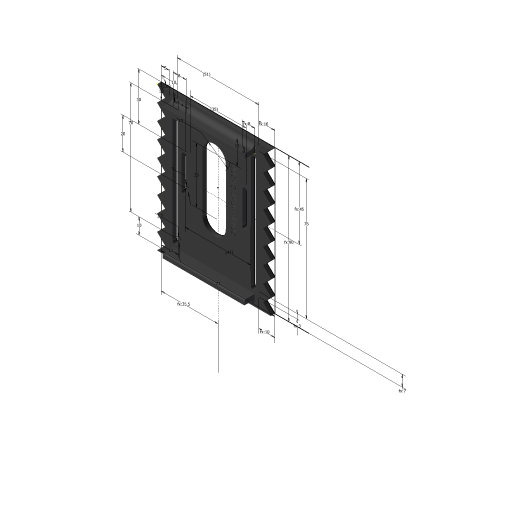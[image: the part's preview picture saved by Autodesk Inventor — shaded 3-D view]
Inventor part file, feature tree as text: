
AUTODESK INVENTOR PART (.ipt)
format: ipt  version: 2023 (Build 270158000, 158)  size: 500,736 bytes
history: native  units: mm
features: extrude x4, sketch x3, fillet x3, other x2
ambient origin geometry x8: Origin, YZ Plane, XZ Plane, XY Plane, X Axis, Y Axis, Z Axis, Center Point
bodies: Solid1 (feature_tree)
feature tree (12):
  sketch  "Sketch1"  dims[d0=71.0mm d1=90.0mm]
  extrude  "Extrusion1"  Depth=90.0mm
  extrude  "Extrusion2"  Depth=5.0mm
  fillet  "Fillet1"  Radius=35.5mm
  extrude  "Extrusion3"  Depth=10.0mm
  sketch  "Sketch2"  dims[d2=45.0deg d3=5.0mm]
  other  "Work Point1"
  other  "Work Point2"
  fillet  "Fillet2"  Radius=10.0mm
  fillet  "Fillet3"  Radius=3.0mm
  extrude  "Extrusion5"  Depth=10.0mm
  sketch  "Sketch3"  dims[d4=90.0mm d6=10.0mm d7=10.0mm d9=10.0mm d11=35.5mm d12=10.0mm d13=10.0mm d14=3.0mm d15=10.0mm d16=3.0mm d17=76.0mm d19=7.0mm d20=3.2mm d21=11.0mm d22=10.0mm d24=51.0mm d25=3.0mm d26=4.0mm d27=30.0mm d28=20.0mm d29=35.0mm d30=41.0mm d31=2.5mm d32=0.0mm d33=9.0mm d34=0.0mm d35=3.0mm d39=35.0mm d40=15.0mm d41=15.0mm d42=0.0mm d43=0.0mm d44=70.0mm d45=45.0mm d48=3.0mm d49=8.0mm d50=8.0mm d51=0.0mm d52=0.0mm d53=5.0mm d54=2.0mm d55=5.0mm d56=8.0mm d57=1.0mm d58=1.0mm d59=0.0mm]
